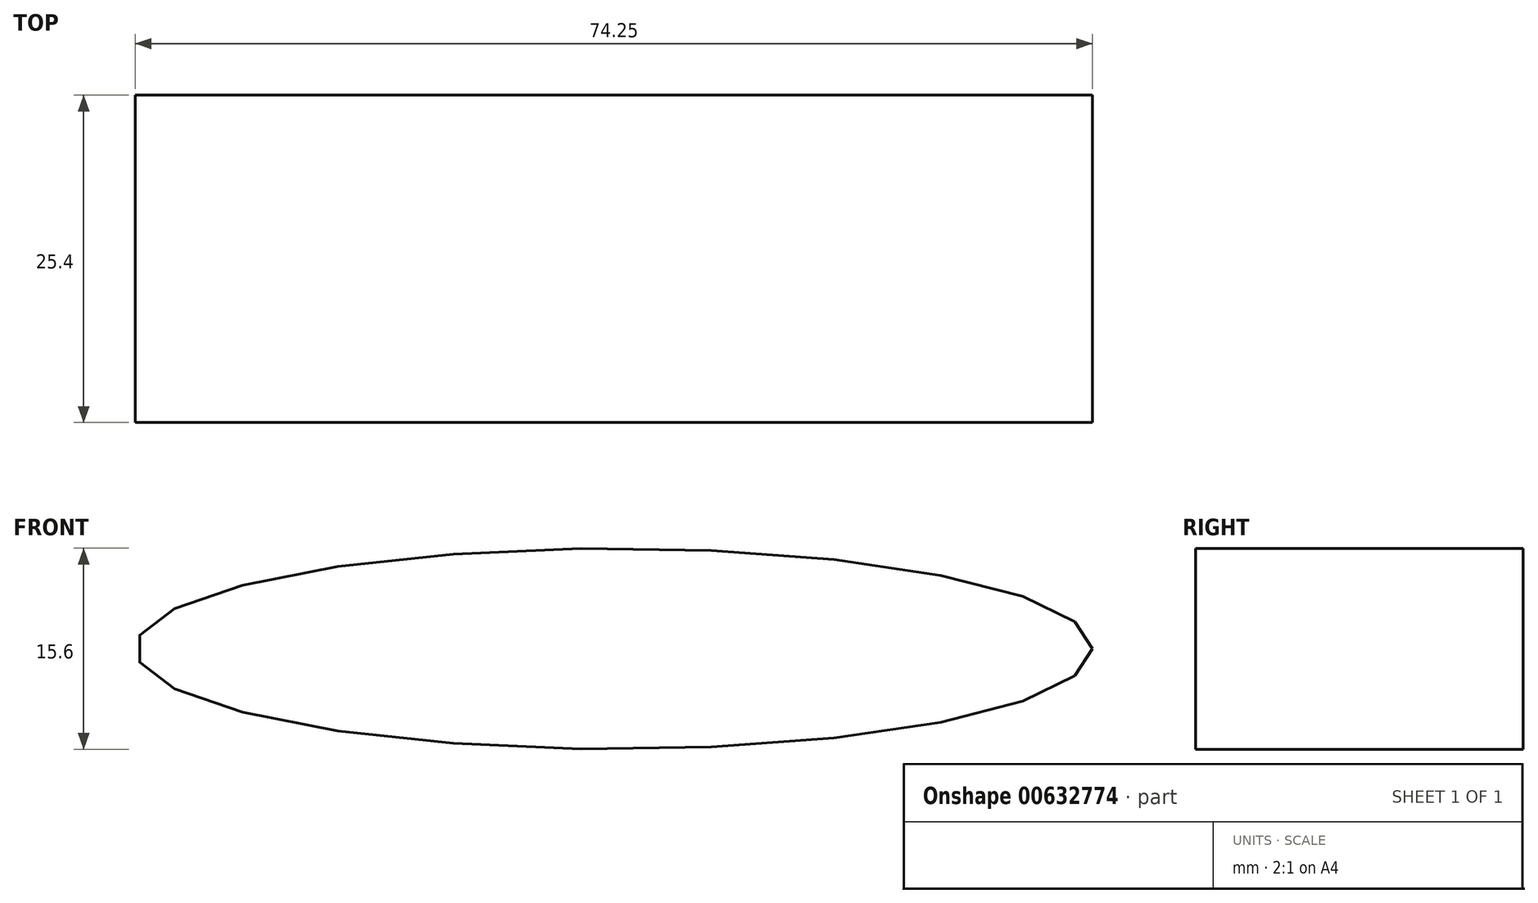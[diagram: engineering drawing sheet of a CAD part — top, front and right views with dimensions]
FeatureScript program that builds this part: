
annotation { "Feature Type Name" : "Feature", "Feature Type Description" : "" }
export const myFeature = defineFeature(function(context is Context, id is Id, definition is map)
    precondition{}
    {
        {
            var Q0;
            Q0=qCreatedBy(makeId("Front.planeOp"),FACE);
            var sketch = newSketch(context, id + "F0", { "sketchPlane" : qUnion([Q0])});
            skEllipse(sketch, "E0", {"center": v(-26.05, 25.47) * mm, "majorRadius": 37.13 * mm, "minorRadius": 7.8 * mm, "majorAxis": v(1, 0)});
            skSolve(sketch);
        }
        {
            var Q0;
            Q0 = qSketchRegion(id + "F0", true);
            extrude(context, id + "F1", {"entities" : qUnion([Q0]), "depth" : 25.4 * mm, "offsetDistance" : 25.4 * mm});
        }
    });
